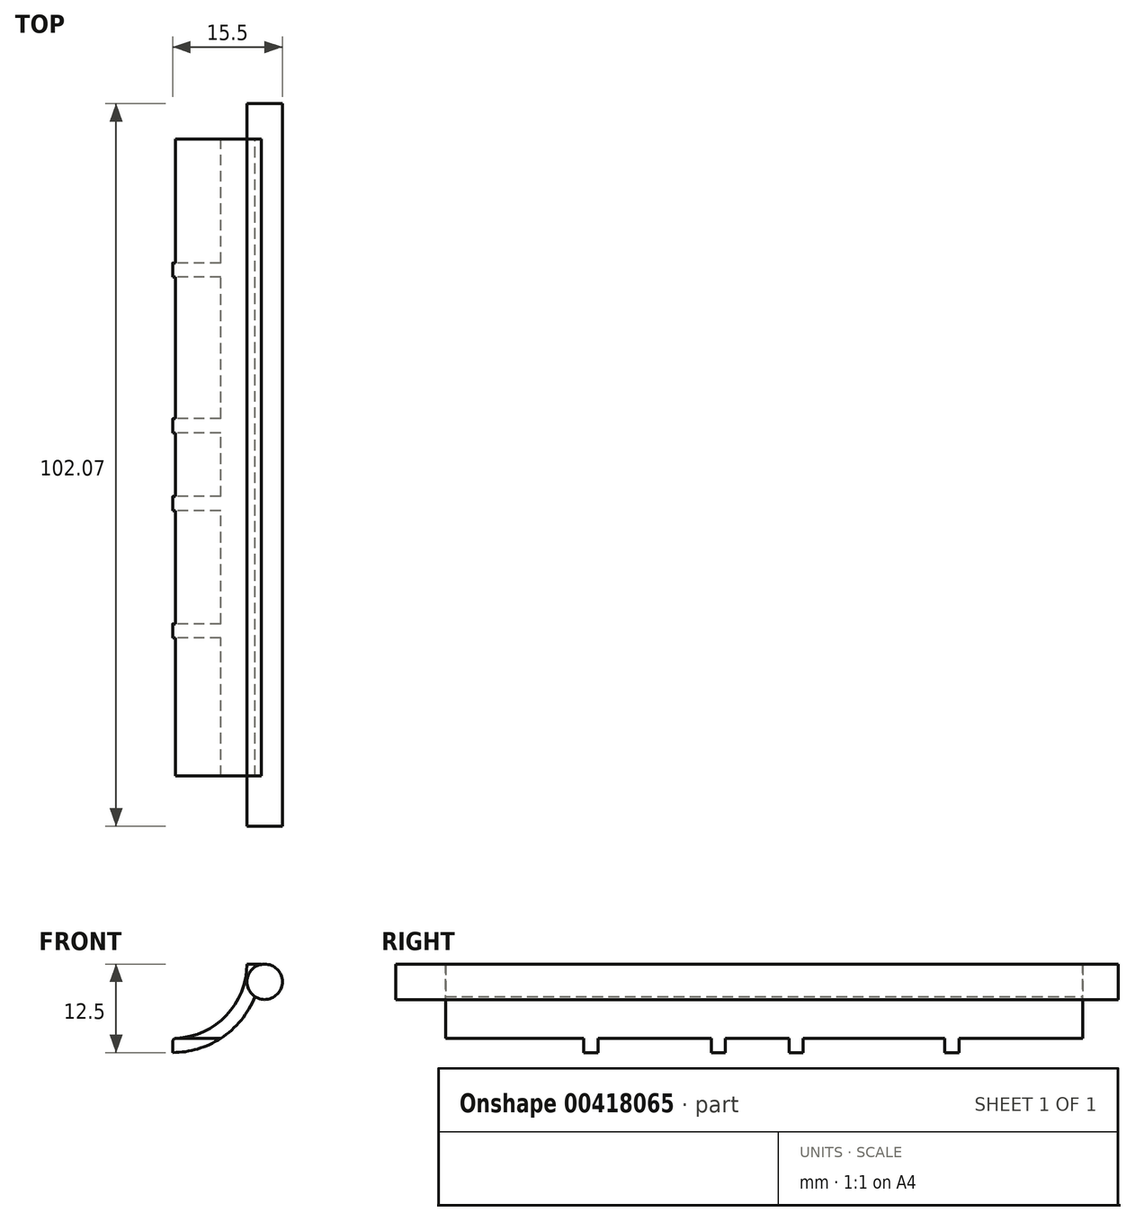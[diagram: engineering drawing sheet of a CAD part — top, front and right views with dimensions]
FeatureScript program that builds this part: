
annotation { "Feature Type Name" : "Feature", "Feature Type Description" : "" }
export const myFeature = defineFeature(function(context is Context, id is Id, definition is map)
    precondition{}
    {
        {
            var Q0;
            Q0=qCreatedBy(makeId("Front.planeOp"),FACE);
            var sketch = newSketch(context, id + "F0", { "sketchPlane" : qUnion([Q0])});
            skArc(sketch, "E0", {"start": v(0, -12.5) * mm, "mid": v(8.84, -8.84) * mm, "end": v(12.5, 0) * mm});
            skLineSegment(sketch, "E1", {"start": v(12.5, 0) * mm, "end": v(10.5, 0) * mm});
            skLineSegment(sketch, "E2", {"start": v(0, -10.99) * mm, "end": v(0, -12.5) * mm});
            skPoint(sketch, "E3.orphan", {"position": v(24.74, 0) * mm});
            skArc(sketch, "E4", {"start": v(0.48, -10.49) * mm, "mid": v(7.6, -7.25) * mm, "end": v(10.5, 0) * mm});
            skPoint(sketch, "E5.visualSharp", {"position": v(0, -10.5) * mm});
            skArc(sketch, "E5.filletArc", {"start": v(0.48, -10.49) * mm, "mid": v(0.14, -10.64) * mm, "end": v(0, -10.99) * mm});
            skSolve(sketch);
        }
        {
            var Q0;
            Q0 = qSketchRegion(id + "F0", true);
            extrude(context, id + "F1", {"entities" : qUnion([Q0]), "depth" : 90 * mm, "offsetDistance" : 25 * mm});
        }
        {
            var Q0;
            Q0=qCreatedBy(makeId("Right.planeOp"),FACE);
            var sketch = newSketch(context, id + "F2", { "sketchPlane" : qUnion([Q0])});
            skLineSegment(sketch, "E6", {"start": v(1.83, -10.5) * mm, "end": v(-17.5, -10.5) * mm});
            skLineSegment(sketch, "E7", {"start": v(-41.5, -10.5) * mm, "end": v(-41.5, -13.92) * mm});
            skLineSegment(sketch, "E8", {"start": v(-19.5, -10.5) * mm, "end": v(-19.5, -13.92) * mm});
            skLineSegment(sketch, "E9", {"start": v(-17.5, -10.5) * mm, "end": v(-17.5, -13.92) * mm});
            skLineSegment(sketch, "E10", {"start": v(-39.5, -10.5) * mm, "end": v(-39.5, -13.92) * mm});
            skLineSegment(sketch, "E11", {"start": v(-70.5, -10.5) * mm, "end": v(-70.5, -13.92) * mm});
            skLineSegment(sketch, "E12", {"start": v(-50.5, -10.5) * mm, "end": v(-50.5, -13.92) * mm});
            skLineSegment(sketch, "E13", {"start": v(-68.5, -10.5) * mm, "end": v(-68.5, -13.92) * mm});
            skLineSegment(sketch, "E14", {"start": v(-52.5, -10.5) * mm, "end": v(-52.5, -13.92) * mm});
            skLineSegment(sketch, "E15", {"start": v(1.83, -14.83) * mm, "end": v(-103.49, -14.83) * mm});
            skPoint(sketch, "E16.orphan", {"position": v(-70.5, -19.82) * mm});
            skPoint(sketch, "E17.orphan", {"position": v(-19.5, -19.82) * mm});
            skLineSegment(sketch, "E18", {"start": v(1.83, -14.83) * mm, "end": v(1.83, -10.5) * mm});
            skLineSegment(sketch, "E19", {"start": v(-103.49, -14.83) * mm, "end": v(-103.28, -10.5) * mm});
            skLineSegment(sketch, "E20", {"start": v(-17.5, -13.92) * mm, "end": v(-19.5, -13.92) * mm});
            skLineSegment(sketch, "E21.trimOffspring", {"start": v(-19.5, -10.5) * mm, "end": v(-39.5, -10.5) * mm});
            skLineSegment(sketch, "E22.trimOffspring", {"start": v(-41.5, -10.5) * mm, "end": v(-50.5, -10.5) * mm});
            skLineSegment(sketch, "E23.trimOffspring", {"start": v(-52.5, -10.5) * mm, "end": v(-68.5, -10.5) * mm});
            skLineSegment(sketch, "E24.trimOffspring", {"start": v(-70.5, -10.5) * mm, "end": v(-103.28, -10.5) * mm});
            skLineSegment(sketch, "E25.trimOffspring", {"start": v(-68.5, -13.92) * mm, "end": v(-70.5, -13.92) * mm});
            skLineSegment(sketch, "E26.trimOffspring", {"start": v(-39.5, -13.92) * mm, "end": v(-52.5, -13.92) * mm});
            skSolve(sketch);
        }
        {
            var Q0;
            Q0 = qSketchRegion(id + "F2", true);
            extrude(context, id + "F3", {"entities" : qUnion([Q0]), "operationType" : NewBodyOperationType.REMOVE, "depth" : 25 * mm, "offsetDistance" : 25 * mm});
        }
        {
            var Q0;
            Q0=qCreatedBy(makeId("Front.planeOp"),FACE);
            var sketch = newSketch(context, id + "F4", { "sketchPlane" : qUnion([Q0])});
            skCircle(sketch, "E27", {"center": v(13, -2.5) * mm, "radius": 2.5 * mm});
            skSolve(sketch);
        }
        {
            var Q0;
            Q0 = qSketchRegion(id + "F4", true);
            extrude(context, id + "F5", {"entities" : qUnion([Q0]), "operationType" : NewBodyOperationType.ADD, "oppositeDirection" : true, "depth" : 5 * mm, "offsetDistance" : 25 * mm});
        }
        {
            var Q0;
            Q0 = qSketchRegion(id + "F4", true);
            extrude(context, id + "F6", {"entities" : qUnion([Q0]), "operationType" : NewBodyOperationType.ADD, "endBound" : BoundingType.THROUGH_ALL, "depth" : 25 * mm, "offsetDistance" : 25 * mm});
        }
    });
